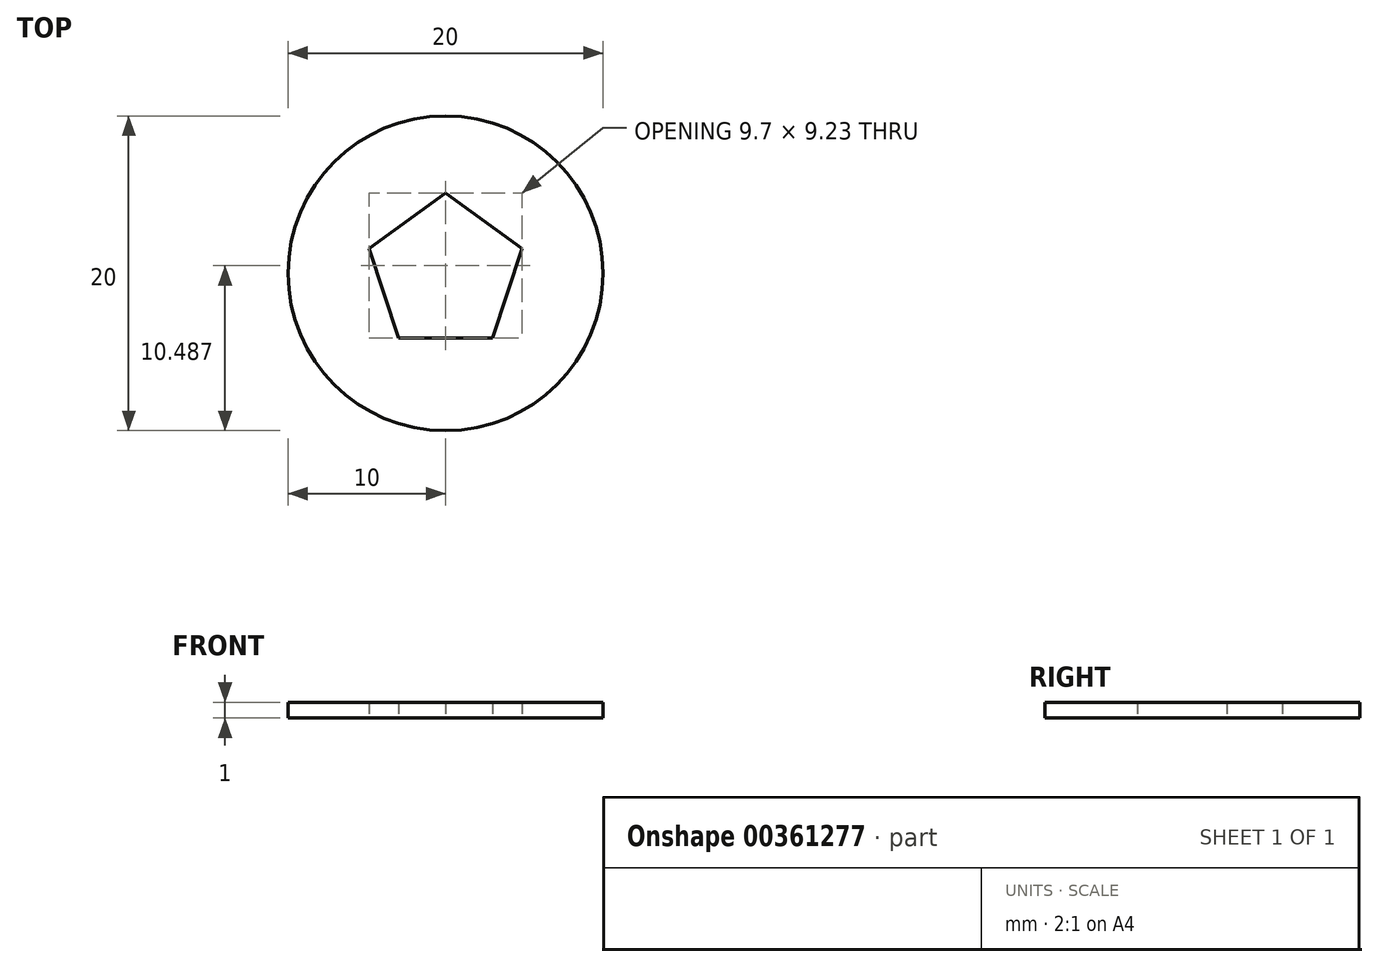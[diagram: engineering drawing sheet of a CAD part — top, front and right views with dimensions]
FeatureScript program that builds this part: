
annotation { "Feature Type Name" : "Feature", "Feature Type Description" : "" }
export const myFeature = defineFeature(function(context is Context, id is Id, definition is map)
    precondition{}
    {
        {
            var Q0;
            Q0=qCreatedBy(makeId("Top.planeOp"),FACE);
            var sketch = newSketch(context, id + "F0", { "sketchPlane" : qUnion([Q0])});
            skCircle(sketch, "E0.cCircle", {"center": v(0, 0) * mm, "radius": 4.13 * mm, "construction": true});
            skLineSegment(sketch, "E0.0", {"start": v(4.85, 1.58) * mm, "end": v(3, -4.13) * mm});
            skLineSegment(sketch, "E0.1", {"start": v(3, -4.13) * mm, "end": v(-3, -4.13) * mm});
            skLineSegment(sketch, "E0.2", {"start": v(-3, -4.13) * mm, "end": v(-4.85, 1.58) * mm});
            skLineSegment(sketch, "E0.3", {"start": v(-4.85, 1.58) * mm, "end": v(0, 5.1) * mm});
            skLineSegment(sketch, "E0.4", {"start": v(0, 5.1) * mm, "end": v(4.85, 1.58) * mm});
            skPoint(sketch, "E0.0.midPoint", {"position": v(3.92, -1.27) * mm});
            skCircle(sketch, "E1", {"center": v(0, 0) * mm, "radius": 10 * mm});
            skSolve(sketch);
        }
        {
            var Q0;
            Q0 = qSketchRegion(id + "F0", true);
            extrude(context, id + "F1", {"entities" : qUnion([Q0]), "depth" : 1 * mm});
        }
    });
